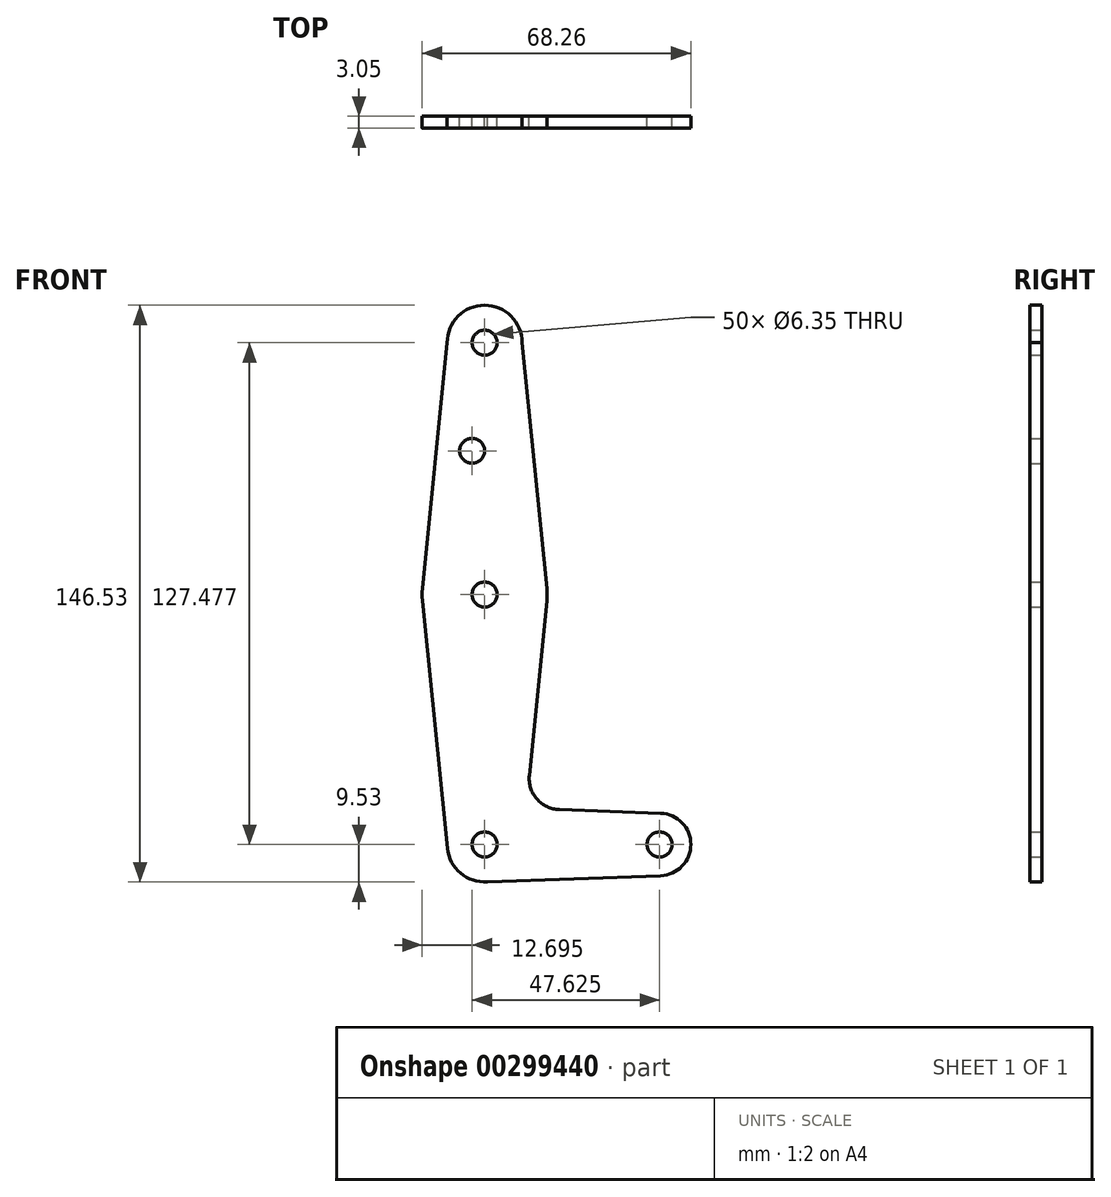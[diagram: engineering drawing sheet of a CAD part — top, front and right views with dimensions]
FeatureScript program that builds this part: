
annotation { "Feature Type Name" : "Feature", "Feature Type Description" : "" }
export const myFeature = defineFeature(function(context is Context, id is Id, definition is map)
    precondition{}
    {
        {
            var Q0;
            Q0=qCreatedBy(makeId("Front.planeOp"),FACE);
            var sketch = newSketch(context, id + "F0", { "sketchPlane" : qUnion([Q0])});
            skCircle(sketch, "E0", {"center": v(0, 0) * mm, "radius": 9.53 * mm});
            skCircle(sketch, "E1", {"center": v(0, 127.48) * mm, "radius": 9.53 * mm});
            skLineSegment(sketch, "E2", {"start": v(0, 0) * mm, "end": v(44.45, 0) * mm, "construction": true});
            skCircle(sketch, "E3", {"center": v(0, 63.5) * mm, "radius": 15.88 * mm});
            skCircle(sketch, "E4", {"center": v(44.45, 0) * mm, "radius": 7.94 * mm});
            skLineSegment(sketch, "E5", {"start": v(18.97, 8.85) * mm, "end": v(44.73, 7.93) * mm});
            skLineSegment(sketch, "E6", {"start": v(0, -9.53) * mm, "end": v(44.73, -7.93) * mm});
            skArc(sketch, "E7.filletArc", {"start": v(11.34, 17.59) * mm, "mid": v(13.26, 11.57) * mm, "end": v(18.97, 8.85) * mm});
            skLineSegment(sketch, "E8", {"start": v(0, 63.5) * mm, "end": v(0, 127.48) * mm, "construction": true});
            skLineSegment(sketch, "E9", {"start": v(0, 63.5) * mm, "end": v(0, 0) * mm, "construction": true});
            skLineSegment(sketch, "E10", {"start": v(9.53, 127.48) * mm, "end": v(15.8, 65.09) * mm});
            skLineSegment(sketch, "E11", {"start": v(15.8, 61.91) * mm, "end": v(11.34, 17.59) * mm});
            skLineSegment(sketch, "E12", {"start": v(-9.53, 127.48) * mm, "end": v(-15.8, 65.09) * mm});
            skLineSegment(sketch, "E13", {"start": v(-15.8, 61.91) * mm, "end": v(-9.48, -0.95) * mm});
            skCircle(sketch, "E14", {"center": v(0, 127.48) * mm, "radius": 3.18 * mm});
            skCircle(sketch, "E15", {"center": v(0, 63.5) * mm, "radius": 3.18 * mm});
            skCircle(sketch, "E16", {"center": v(0, 0) * mm, "radius": 3.18 * mm});
            skCircle(sketch, "E17", {"center": v(44.45, 0) * mm, "radius": 3.18 * mm});
            skCircle(sketch, "E18", {"center": v(-3.18, 100.03) * mm, "radius": 3.18 * mm});
            skSolve(sketch);
        }
        {
            var Q0;
            Q0 = qSketchRegion(id + "F0", true);
            extrude(context, id + "F1", {"entities" : qUnion([Q0]), "depth" : 3.05 * mm});
        }
    });
